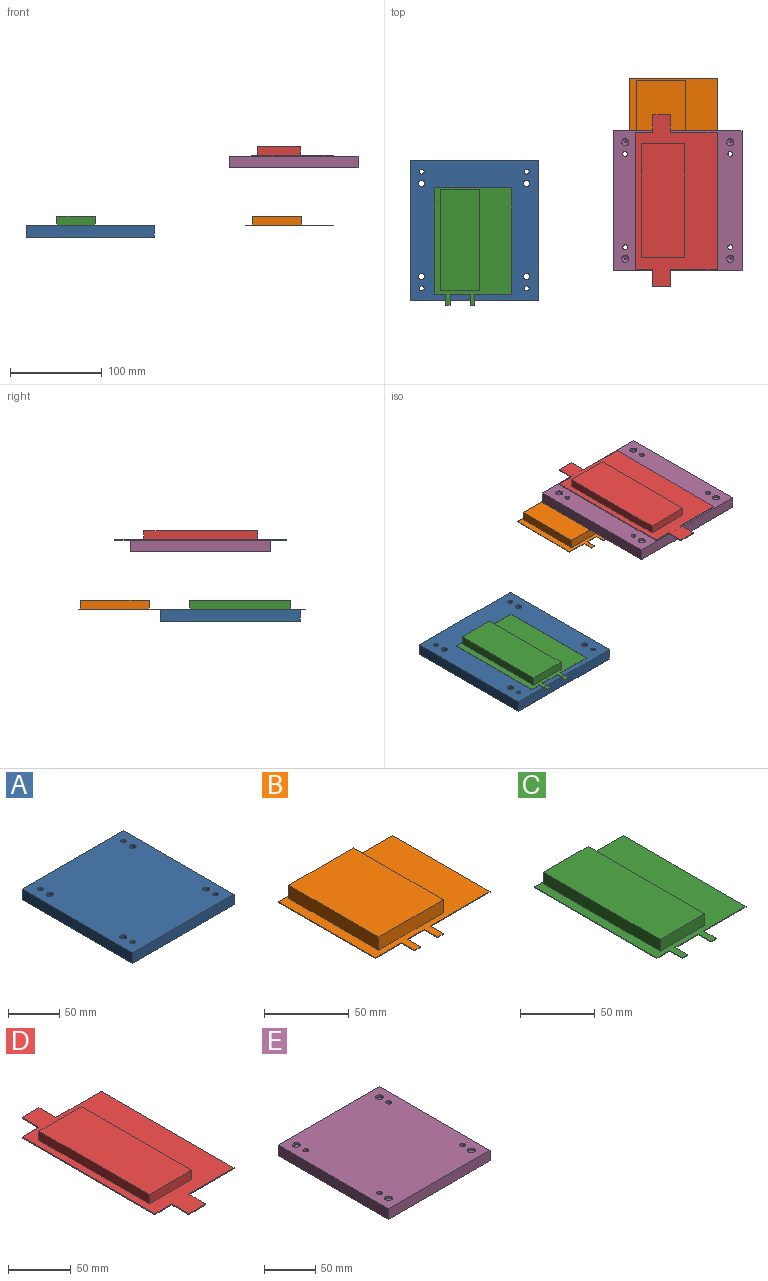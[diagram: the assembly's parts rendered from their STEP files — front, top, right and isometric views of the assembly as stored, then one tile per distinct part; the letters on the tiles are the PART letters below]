
ASSEMBLY  parts=5 mates=3
PART A: 14 faces, bbox 139.7x152.4x12.7 mm
  f0: plane 139.7x12.7mm, normal (0,-1,0), area 1774.2mm2, adj f1,f3,f4,f5
  f1: plane 152.4x12.7mm, normal (1,0,0), area 1935.5mm2, adj f0,f2,f4,f5
  f2: plane 139.7x12.7mm, normal (0,1,0), area 1774.2mm2, adj f1,f3,f4,f5
  f3: plane 152.4x12.7mm, normal (-1,0,0), area 1935.5mm2, adj f0,f2,f4,f5
  f4: plane 152.4x139.7mm, normal (0,0,1), area 21054.9mm2, adj f0,f1,f2,f3,f6,f7,f8,f9
  f5: plane 152.4x139.7mm, normal (0,0,-1), area 21054.9mm2, adj f0,f1,f2,f3,f6,f7,f8,f9
  f6: cylinder r=2.71mm len=12.7mm, axis (0,0,-1), area 215.9mm2, adj f4,f5
  f7: cylinder r=2.71mm len=12.7mm, axis (0,0,-1), area 215.9mm2, adj f4,f5
  f8: cylinder r=2.71mm len=12.7mm, axis (0,0,-1), area 215.9mm2, adj f4,f5
  f9: cylinder r=2.71mm len=12.7mm, axis (0,0,-1), area 215.9mm2, adj f4,f5
  f10: cylinder r=3.38mm len=12.7mm, axis (0,0,-1), area 269.6mm2, adj f4,f5
  f11: cylinder r=3.38mm len=12.7mm, axis (0,0,-1), area 269.6mm2, adj f4,f5
  f12: cylinder r=3.38mm len=12.7mm, axis (0,0,-1), area 269.6mm2, adj f4,f5
  f13: cylinder r=3.38mm len=12.7mm, axis (0,0,-1), area 269.6mm2, adj f4,f5
PART B: 19 faces, bbox 96x92x10 mm
  f0: plane 54x9.5mm, normal (0,-1,0), area 513mm2, adj f1,f3,f4,f17
  f1: plane 75x9.5mm, normal (1,0,0), area 712.5mm2, adj f0,f2,f4,f17
  f2: plane 54x9.5mm, normal (0,1,0), area 513mm2, adj f1,f3,f4,f17
  f3: plane 75x9.5mm, normal (-1,0,0), area 712.5mm2, adj f0,f2,f4,f17
  f4: plane 75x54mm, normal (0,0,1), area 4050mm2, adj f0,f1,f2,f3
  f5: plane 11x0.5mm, normal (-1,0,0), area 5.5mm2, adj f6,f16,f17,f18
  f6: plane 5x0.5mm, normal (0,-1,0), area 2.5mm2, adj f5,f7,f17,f18
  f7: plane 11x0.5mm, normal (1,0,0), area 5.5mm2, adj f6,f8,f17,f18
  f8: plane 14x0.5mm, normal (0,-1,0), area 7mm2, adj f7,f9,f17,f18
  f9: plane 11x0.5mm, normal (-1,0,0), area 5.5mm2, adj f8,f10,f17,f18
  f10: plane 5x0.5mm, normal (0,-1,0), area 2.5mm2, adj f9,f11,f17,f18
  f11: plane 11x0.5mm, normal (1,0,0), area 5.5mm2, adj f10,f12,f17,f18
  f12: plane 50x0.5mm, normal (0,-1,0), area 25mm2, adj f11,f13,f17,f18
  f13: plane 81x0.5mm, normal (1,0,0), area 40.5mm2, adj f12,f14,f17,f18
  f14: plane 96x0.5mm, normal (0,1,0), area 48mm2, adj f13,f15,f17,f18
  f15: plane 81x0.5mm, normal (-1,0,0), area 40.5mm2, adj f14,f16,f17,f18
  f16: plane 22x0.5mm, normal (0,-1,0), area 11mm2, adj f5,f15,f17,f18
  f17: plane 96x92mm, normal (0,0,1), area 3836mm2, adj f0,f1,f2,f3,f5,f6,f7,f8
  f18: plane 96x92mm, normal (0,0,-1), area 7886mm2, adj f5,f6,f7,f8,f9,f10,f11,f12
PART C: 19 faces, bbox 84x128x10 mm
  f0: plane 42x9.5mm, normal (0,-1,0), area 399mm2, adj f1,f3,f4,f17
  f1: plane 110x9.5mm, normal (1,0,0), area 1045mm2, adj f0,f2,f4,f17
  f2: plane 42x9.5mm, normal (0,1,0), area 399mm2, adj f1,f3,f4,f17
  f3: plane 110x9.5mm, normal (-1,0,0), area 1045mm2, adj f0,f2,f4,f17
  f4: plane 110x42mm, normal (0,0,1), area 4620mm2, adj f0,f1,f2,f3
  f5: plane 12x0.5mm, normal (-1,0,0), area 6mm2, adj f6,f16,f17,f18
  f6: plane 5x0.5mm, normal (0,-1,0), area 2.5mm2, adj f5,f7,f17,f18
  f7: plane 12x0.5mm, normal (1,0,0), area 6mm2, adj f6,f8,f17,f18
  f8: plane 22x0.5mm, normal (0,-1,0), area 11mm2, adj f7,f9,f17,f18
  f9: plane 12x0.5mm, normal (-1,0,0), area 6mm2, adj f8,f10,f17,f18
  f10: plane 5x0.5mm, normal (0,-1,0), area 2.5mm2, adj f9,f11,f17,f18
  f11: plane 12x0.5mm, normal (1,0,0), area 6mm2, adj f10,f12,f17,f18
  f12: plane 40x0.5mm, normal (0,-1,0), area 20mm2, adj f11,f13,f17,f18
  f13: plane 116x0.5mm, normal (1,0,0), area 58mm2, adj f12,f14,f17,f18
  f14: plane 84x0.5mm, normal (0,1,0), area 42mm2, adj f13,f15,f17,f18
  f15: plane 116x0.5mm, normal (-1,0,0), area 58mm2, adj f14,f16,f17,f18
  f16: plane 12x0.5mm, normal (0,-1,0), area 6mm2, adj f5,f15,f17,f18
  f17: plane 128x84mm, normal (0,0,1), area 5244mm2, adj f0,f1,f2,f3,f5,f6,f7,f8
  f18: plane 128x84mm, normal (0,0,-1), area 9864mm2, adj f5,f6,f7,f8,f9,f10,f11,f12
PART D: 19 faces, bbox 89x187.3x10 mm
  f0: plane 47.63x9mm, normal (0,1,0), area 428.6mm2, adj f1,f3,f4,f17
  f1: plane 123.83x9mm, normal (-1,0,0), area 1114.4mm2, adj f0,f2,f4,f17
  f2: plane 47.63x9mm, normal (0,-1,0), area 428.6mm2, adj f1,f3,f4,f17
  f3: plane 123.83x9mm, normal (1,0,0), area 1114.4mm2, adj f0,f2,f4,f17
  f4: plane 123.83x47.63mm, normal (0,0,1), area 5897.2mm2, adj f0,f1,f2,f3
  f5: plane 19.05x1mm, normal (1,0,0), area 19mm2, adj f6,f16,f17,f18
  f6: plane 50.88x1mm, normal (0,-1,0), area 50.9mm2, adj f5,f7,f17,f18
  f7: plane 149.23x1mm, normal (1,0,0), area 149.2mm2, adj f6,f8,f17,f18
  f8: plane 50.88x1mm, normal (0,1,0), area 50.9mm2, adj f7,f9,f17,f18
  f9: plane 19.05x1mm, normal (1,0,0), area 19mm2, adj f8,f10,f17,f18
  f10: plane 19.05x1mm, normal (0,1,0), area 19mm2, adj f9,f11,f17,f18
  f11: plane 19.05x1mm, normal (-1,0,0), area 19mm2, adj f10,f12,f17,f18
  f12: plane 19.05x1mm, normal (0,1,0), area 19mm2, adj f11,f13,f17,f18
  f13: plane 149.23x1mm, normal (-1,0,0), area 149.2mm2, adj f12,f14,f17,f18
  f14: plane 19.05x1mm, normal (0,-1,0), area 19mm2, adj f13,f15,f17,f18
  f15: plane 19.05x1mm, normal (-1,0,0), area 19mm2, adj f14,f16,f17,f18
  f16: plane 19.05x1mm, normal (0,-1,0), area 19.1mm2, adj f5,f15,f17,f18
  f17: plane 187.33x88.98mm, normal (0,0,1), area 8106.1mm2, adj f0,f1,f2,f3,f5,f6,f7,f8
  f18: plane 187.33x88.98mm, normal (0,0,-1), area 14003.3mm2, adj f5,f6,f7,f8,f9,f10,f11,f12
PART E: 26 faces, bbox 139.7x152.4x12.7 mm
  f0: cone r=0mm half-angle=59deg, axis (0,0,1), area 52.4mm2, adj f10,f24
  f1: cone r=0mm half-angle=59deg, axis (0,0,1), area 52.4mm2, adj f11,f22
  f2: cone r=0mm half-angle=59deg, axis (0,0,1), area 52.4mm2, adj f12,f20
  f3: cone r=0mm half-angle=59deg, axis (0,0,1), area 52.4mm2, adj f13,f18
  f4: plane 139.7x12.7mm, normal (0,-1,0), area 1774.2mm2, adj f5,f7,f8,f9
  f5: plane 152.4x12.7mm, normal (1,0,0), area 1935.5mm2, adj f4,f6,f8,f9
  f6: plane 139.7x12.7mm, normal (0,1,0), area 1774.2mm2, adj f5,f7,f8,f9
  f7: plane 152.4x12.7mm, normal (-1,0,0), area 1935.5mm2, adj f4,f6,f8,f9
  f8: plane 152.4x139.7mm, normal (0,0,1), area 21015.9mm2, adj f4,f5,f6,f7,f10,f11,f12,f13
  f9: plane 152.4x139.7mm, normal (0,0,-1), area 20810.4mm2, adj f4,f5,f6,f7,f14,f15,f16,f17
  f10: cylinder r=3.81mm len=7.62mm, axis (0,0,1), area 60.8mm2, adj f0,f8
  f11: cylinder r=3.81mm len=7.62mm, axis (0,0,1), area 60.8mm2, adj f1,f8
  f12: cylinder r=3.81mm len=7.62mm, axis (0,0,1), area 60.8mm2, adj f2,f8
  f13: cylinder r=3.81mm len=7.62mm, axis (0,0,1), area 60.8mm2, adj f3,f8
  f14: cylinder r=2.71mm len=12.7mm, axis (0,0,-1), area 215.9mm2, adj f8,f9
  f15: cylinder r=2.71mm len=12.7mm, axis (0,0,-1), area 215.9mm2, adj f8,f9
  f16: cylinder r=2.71mm len=12.7mm, axis (0,0,-1), area 215.9mm2, adj f8,f9
  f17: cylinder r=2.71mm len=12.7mm, axis (0,0,-1), area 215.9mm2, adj f8,f9
  f18: cone r=0mm half-angle=59deg, axis (0,0,-1), area 112.4mm2, adj f3,f19
  f19: cylinder r=5.56mm len=11.11mm, axis (0,0,-1), area 177.3mm2, adj f9,f18
  f20: cone r=0mm half-angle=59deg, axis (0,0,-1), area 112.4mm2, adj f2,f21
  f21: cylinder r=5.56mm len=11.11mm, axis (0,0,-1), area 177.3mm2, adj f9,f20
  f22: cone r=0mm half-angle=59deg, axis (0,0,-1), area 112.4mm2, adj f1,f23
  f23: cylinder r=5.56mm len=11.11mm, axis (0,0,-1), area 177.3mm2, adj f9,f22
  f24: cone r=0mm half-angle=59deg, axis (0,0,-1), area 112.4mm2, adj f0,f25
  f25: cylinder r=5.56mm len=11.11mm, axis (0,0,-1), area 177.3mm2, adj f9,f24
PLACE A t=(-148.48,-8.65,-34.08)mm
PLACE B t=(54.75,116.81,-21.38)mm
PLACE C t=(-163.79,-19.75,-21.38)mm
PLACE D t=(57.14,23.2,54.18)mm
PLACE E t=(73.16,23.32,41.48)mm
MATE planar B.f18 <-> A.f4  axis (0,0,-1) through (68.56,115.17,-21.38)mm
MATE planar D.f18 <-> E.f8  axis (0,0,-1) through (70.64,23.2,54.18)mm
MATE planar C.f18 <-> A.f4  axis (0,0,-1) through (-149.96,-21.53,-21.38)mm
